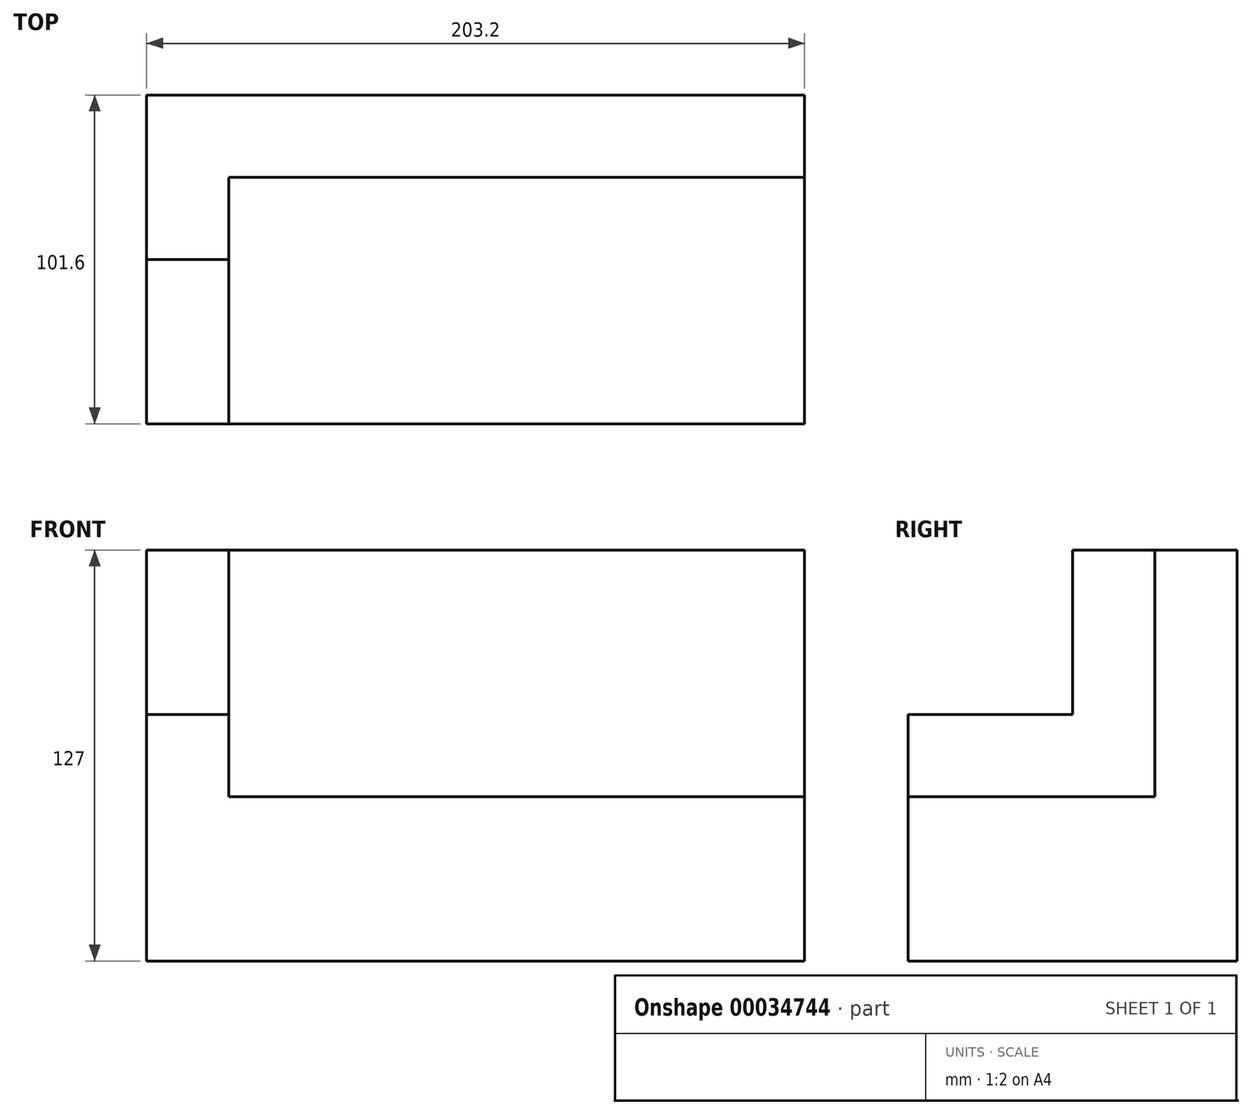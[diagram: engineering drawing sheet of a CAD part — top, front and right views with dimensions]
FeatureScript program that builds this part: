
annotation { "Feature Type Name" : "Feature", "Feature Type Description" : "" }
export const myFeature = defineFeature(function(context is Context, id is Id, definition is map)
    precondition{}
    {
        {
            var Q0;
            Q0=qCreatedBy(makeId("Top.planeOp"),FACE);
            var sketch = newSketch(context, id + "F0", { "sketchPlane" : qUnion([Q0])});
            skLineSegment(sketch, "E0.bottom", {"start": v(-69.5, 54.22) * mm, "end": v(133.7, 54.22) * mm});
            skLineSegment(sketch, "E0.top", {"start": v(-69.5, -47.38) * mm, "end": v(133.7, -47.38) * mm});
            skLineSegment(sketch, "E0.left", {"start": v(-69.5, 54.22) * mm, "end": v(-69.5, -47.38) * mm});
            skLineSegment(sketch, "E0.right", {"start": v(133.7, 54.22) * mm, "end": v(133.7, -47.38) * mm});
            skSolve(sketch);
        }
        {
            var Q0;
            Q0=makeQuery(id+"F0.imprint","IMPRINT",FACE,{"disambiguationData":[TD([[makeQuery(id+"F0.imprint","IMPRINT",EDGE,{"derivedFrom":sQuery(id+"F0.wireOp",EDGE,"E0.bottom")}),-1.0]])]});
            extrude(context, id + "F1", {"entities" : qUnion([Q0]), "depth" : 127 * mm});
        }
        {
            var Q0;
            Q0=makeQuery(id+"F1.opExtrude","CAP_FACE",FACE,{"disambiguationData":[OSD([sQuery(id+"F0.wireOp",EDGE,"E0.bottom"),sQuery(id+"F0.wireOp",EDGE,"E0.top"),sQuery(id+"F0.wireOp",EDGE,"E0.left"),sQuery(id+"F0.wireOp",EDGE,"E0.right")])],"isStart":false});
            var sketch = newSketch(context, id + "F2", { "sketchPlane" : qUnion([Q0])});
            skLineSegment(sketch, "E1.bottom", {"start": v(133.7, -47.38) * mm, "end": v(-44.1, -47.38) * mm});
            skLineSegment(sketch, "E1.top", {"start": v(133.7, 28.82) * mm, "end": v(-44.1, 28.82) * mm});
            skLineSegment(sketch, "E1.left", {"start": v(133.7, -47.38) * mm, "end": v(133.7, 28.82) * mm});
            skLineSegment(sketch, "E1.right", {"start": v(-44.1, -47.38) * mm, "end": v(-44.1, 28.82) * mm});
            skSolve(sketch);
        }
        {
            var Q0;
            Q0 = qSketchRegion(id + "F2", true);
            extrude(context, id + "F3", {"entities" : qUnion([Q0]), "operationType" : NewBodyOperationType.REMOVE, "oppositeDirection" : true, "depth" : 76.2 * mm});
        }
        {
            var Q0;
            Q0=makeQuery(id+"F1.opExtrude","CAP_FACE",FACE,{"disambiguationData":[OSD([sQuery(id+"F0.wireOp",EDGE,"E0.bottom"),sQuery(id+"F0.wireOp",EDGE,"E0.top"),sQuery(id+"F0.wireOp",EDGE,"E0.left"),sQuery(id+"F0.wireOp",EDGE,"E0.right")])],"isStart":false});
            var sketch = newSketch(context, id + "F4", { "sketchPlane" : qUnion([Q0])});
            skLineSegment(sketch, "E2.bottom", {"start": v(-69.5, -47.38) * mm, "end": v(-44.1, -47.38) * mm});
            skLineSegment(sketch, "E2.top", {"start": v(-69.5, 3.42) * mm, "end": v(-44.1, 3.42) * mm});
            skLineSegment(sketch, "E2.left", {"start": v(-69.5, -47.38) * mm, "end": v(-69.5, 3.42) * mm});
            skLineSegment(sketch, "E2.right", {"start": v(-44.1, -47.38) * mm, "end": v(-44.1, 3.42) * mm});
            skSolve(sketch);
        }
        {
            var Q0;
            Q0 = qSketchRegion(id + "F4", true);
            extrude(context, id + "F5", {"entities" : qUnion([Q0]), "operationType" : NewBodyOperationType.REMOVE, "oppositeDirection" : true, "depth" : 50.8 * mm});
        }
    });
